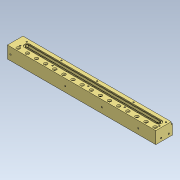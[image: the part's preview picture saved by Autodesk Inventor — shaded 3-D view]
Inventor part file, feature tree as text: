
AUTODESK INVENTOR PART (.ipt)
format: ipt  version: 2022.4 (Build 264492010, 492A)  size: 526,848 bytes
history: native  units: in
note: dims shown in document units (in); Inventor stores cm internally (conversion verified against a paired STEP export)
features: hole x12, sketch x10, extrude x4, other x1
ambient origin geometry x8: Origin, YZ Plane, XZ Plane, XY Plane, X Axis, Y Axis, Z Axis, Center Point
bodies: Solid1 (feature_tree)
feature tree (27):
  sketch  "Sketch:MM: main inlet"  dims[d160=0.245in d161=0.055in]
  extrude  "Ex: main"  Depth=0.5635in
  hole  "Hole: main inlet: 1/8" NPT thread"  [1 undecoded]
  hole  "Hole: main inlet: tube"  [1 undecoded]
  sketch  "Sketch:MM: prop valves"  dims[d162=0.5635in d164=0.0in]
  sketch  "Sketch:MM: prop valve cutout"  dims[d168=0.75in d171=0.5635in]
  hole  "Hole: propValve: inlet"  [1 undecoded]
  hole  "Hole: propValve: outlet"  [1 undecoded]
  hole  "Hole: propValve: 4-40 thread"  [1 undecoded]
  extrude  "Ex: prop valve cutout"  Depth=0.75in
  sketch  "Sketch:MM: flow sensor"  dims[d173=0.0in d192=0.75in]
  sketch  "Sketch:MM: MMC screws"  dims[d195=0.5635in d196=0.28in d197=0.0in]
  hole  "Hole: flowSensor"  [1 undecoded]
  hole  "Hole: MMC screws: 4-40 through hole"  [1 undecoded]
  sketch  "Sketch:MM: bath & TC screws"  dims[d232=5.25in d319=0.3in]
  extrude  "Ex: bath"  TaperAngle=0.0deg  [1 undecoded]
  extrude  "Ex: bath: o-ring"  Depth=0.5in
  hole  "Hole: TC screws: 4-40 thread"  [1 undecoded]
  sketch  "Sketch:MM: MP screws"  dims[d353=0.375in d354=0.25in d355=0.5635in d357=0.0in d361=0.375in d362=0.25in d363=0.5635in d365=0.0in d387=0.75in d388=0.375in d389=0.25in d390=0.5635in d392=0.0in d397=0.0849in d399=0.375in d400=0.25in d401=0.5635in d403=0.0in d421=0.0849in d423=0.375in d424=0.25in d425=0.5635in d427=0.0in d428=0.313in d429=0.2726in d430=0.0246in d431=0.3269in d432=0.375in d433=0.25in d434=0.5635in d436=0.0in d439=0.0in d447=0.0849in d449=0.375in d450=0.25in d451=0.5635in d453=0.0in d55=1.0in d56=1.0in d57=1.0in d58=0.15in d59=0.25in d60=0.375in d61=0.5635in d62=0.75in d63=0.8108in d64=0.0625in d65=0.75in d66=0.375in d106=0.5in d107=0.0344in d108=0.5in d109=0.0344in d252=1.0in d253=1.0in d254=1.0in d255=0.15in d256=0.25in d257=0.375in d258=0.5635in d259=0.75in d260=0.8108in d261=0.0625in d262=0.75in d263=0.375in d394=1.0in d395=1.0in d396=1.0in d398=0.25in d402=0.8108in d404=0.75in d405=0.375in d437=1.0in d438=1.0in d440=0.15in d441=0.129in d442=0.375in d443=0.5635in d444=0.75in d445=0.8108in d446=0.0625in d448=0.375in]
  sketch  "Sketch:MM: MP screws:2"  dims[d149=0.0in d152=0.75in]
  hole  "Hole: MP screws: 4-40 thread"  [1 undecoded]
  hole  "Hole: MP screws: 4-40 thread:2"  [1 undecoded]
  sketch  "Sketch:MM: mounting screws:1"  dims[d144=0.75in d147=0.5635in]
  sketch  "Sketch:MM: mounting screws:2"  dims[d155=0.5635in d157=0.0in]
  hole  "Hole: mounting screws:1: 4-40 thread"  [1 undecoded]
  hole  "Hole: mounting screws:2: 4-40 thread"  [1 undecoded]
  other  "MM front face"
note: 13 required parameter values undecoded (feature->parameter linkage not recoverable at this tier; creation-order binding heuristic only, values carry confidence <= 0.55)
